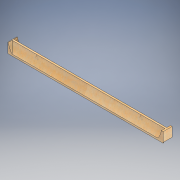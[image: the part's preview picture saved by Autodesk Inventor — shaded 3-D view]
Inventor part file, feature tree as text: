
AUTODESK INVENTOR PART (.ipt)
format: ipt  version: 2022.2 (Build 262287010, 287A)  size: 189,952 bytes
history: native  units: in
note: dims shown in document units (in); Inventor stores cm internally (conversion verified against a paired STEP export)
features: direct_edit x1, extrude x1, sketch x1, projected_geometry x1, other x1, revolve x1
ambient origin geometry x8: Origin, YZ Plane, XZ Plane, XY Plane, X Axis, Y Axis, Z Axis, Center Point
bodies: Solid1 (feature_tree)
feature tree (6):
  direct_edit  "Direct Edit1"
  extrude  "Extrusion1"  Depth=1.0in TaperAngle=0.0deg
  sketch  "Sketch1"  dims[d0=-1.2368in d1=1.0in d2=0.0in]
  projected_geometry  "Projected Loop1"
  other  "Transom (R) (1)"
  revolve  "Rotate1"  [1 undecoded]
note: 1 required parameter value undecoded (feature->parameter linkage not recoverable at this tier; creation-order binding heuristic only, values carry confidence <= 0.55)
